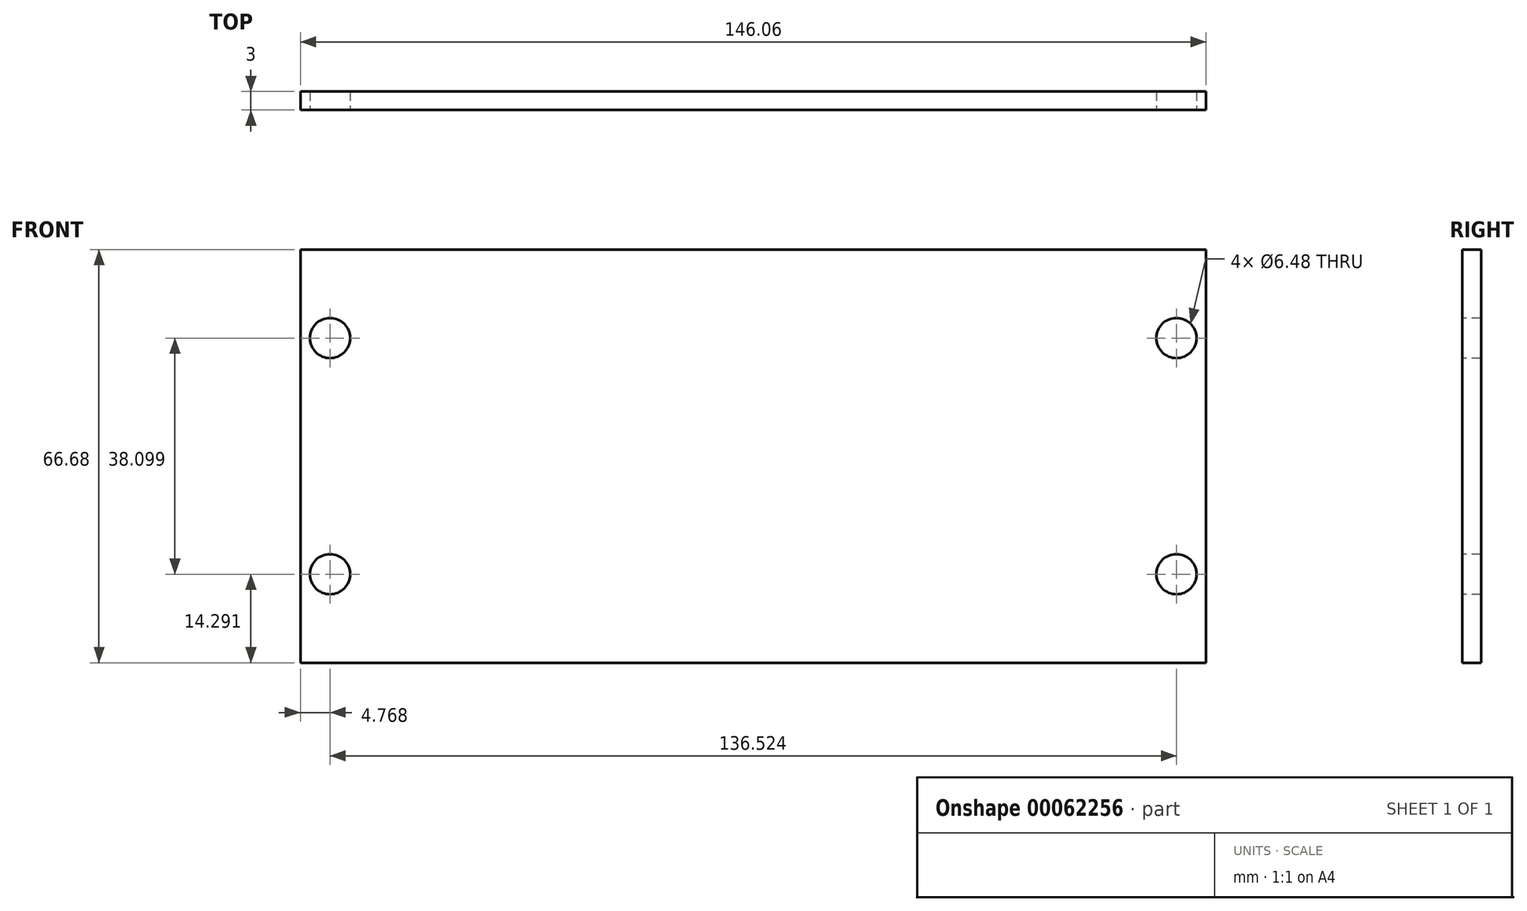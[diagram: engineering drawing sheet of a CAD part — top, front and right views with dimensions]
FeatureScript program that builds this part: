
annotation { "Feature Type Name" : "Feature", "Feature Type Description" : "" }
export const myFeature = defineFeature(function(context is Context, id is Id, definition is map)
    precondition{}
    {
        {
            var Q0;
            Q0=qCreatedBy(makeId("Front.planeOp"),FACE);
            var sketch = newSketch(context, id + "F0", { "sketchPlane" : qUnion([Q0])});
            skCircle(sketch, "E0", {"center": v(68.26, 19.05) * mm, "radius": 3.24 * mm});
            skCircle(sketch, "E1", {"center": v(68.26, -19.05) * mm, "radius": 3.24 * mm});
            skLineSegment(sketch, "E2", {"start": v(73.03, -33.34) * mm, "end": v(73.03, 33.34) * mm});
            skLineSegment(sketch, "E3", {"start": v(-73.03, 33.34) * mm, "end": v(73.03, 33.34) * mm});
            skLineSegment(sketch, "E4", {"start": v(-73.03, -33.34) * mm, "end": v(-73.03, 33.34) * mm});
            skLineSegment(sketch, "E5", {"start": v(73.03, -33.34) * mm, "end": v(-73.03, -33.34) * mm});
            skCircle(sketch, "E6", {"center": v(-68.26, -19.05) * mm, "radius": 3.24 * mm});
            skCircle(sketch, "E7", {"center": v(-68.26, 19.05) * mm, "radius": 3.24 * mm});
            skSolve(sketch);
        }
        {
            var Q0;
            Q0=makeQuery(id+"F0.imprint","IMPRINT",FACE,{"disambiguationData":[TD([[makeQuery(id+"F0.imprint","IMPRINT",EDGE,{"derivedFrom":sQuery(id+"F0.wireOp",EDGE,"E3")}),-1.0]])]});
            extrude(context, id + "F1", {"entities" : qUnion([Q0]), "oppositeDirection" : true, "depth" : 3 * mm, "offsetDistance" : 25 * mm});
        }
    });
